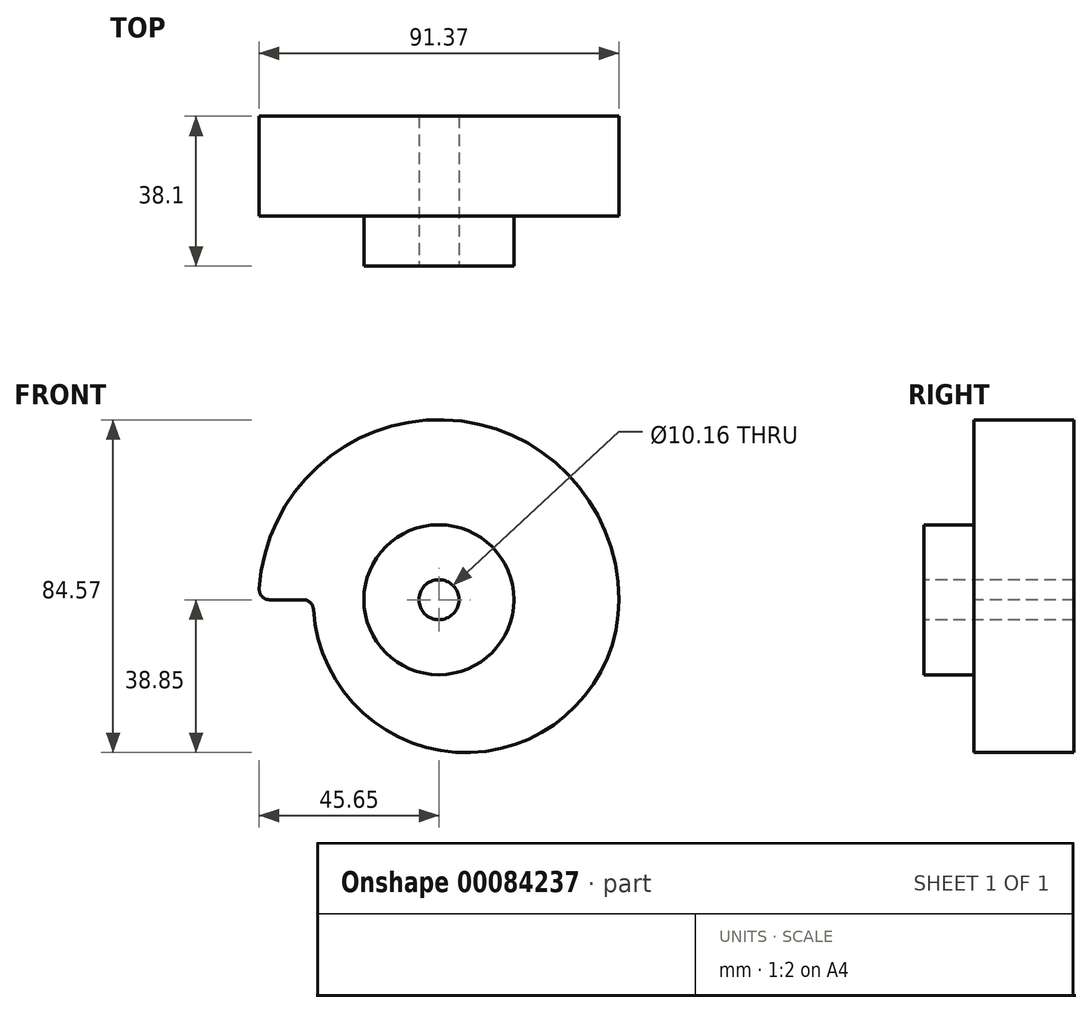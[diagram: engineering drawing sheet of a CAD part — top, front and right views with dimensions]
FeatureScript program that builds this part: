
annotation { "Feature Type Name" : "Feature", "Feature Type Description" : "" }
export const myFeature = defineFeature(function(context is Context, id is Id, definition is map)
    precondition{}
    {
        {
            var Q0;
            Q0=qCreatedBy(makeId("Front.planeOp"),FACE);
            var sketch = newSketch(context, id + "F0", { "sketchPlane" : qUnion([Q0])});
            skLineSegment(sketch, "E0", {"start": v(0, 0) * mm, "end": v(45.72, 0) * mm, "construction": true});
            skArc(sketch, "E1", {"start": v(45.72, 0) * mm, "mid": v(0, 45.72) * mm, "end": v(-45.72, 0) * mm});
            skArc(sketch, "E2", {"start": v(45.72, 0) * mm, "mid": v(6.87, -38.85) * mm, "end": v(-31.98, 0) * mm});
            skLineSegment(sketch, "E3", {"start": v(-31.98, 0) * mm, "end": v(0, 0) * mm, "construction": true});
            skLineSegment(sketch, "E4", {"start": v(-45.72, 0) * mm, "end": v(-31.98, 0) * mm});
            skSolve(sketch);
        }
        {
            var Q0;
            Q0=makeQuery(id+"F0.imprint","IMPRINT",FACE,{"disambiguationData":[TD([[makeQuery(id+"F0.imprint","IMPRINT",EDGE,{"derivedFrom":sQuery(id+"F0.wireOp",EDGE,"E1")}),1.0]])]});
            extrude(context, id + "F1", {"entities" : qUnion([Q0]), "depth" : 25.4 * mm});
        }
        {
            var Q0;
            Q0=makeQuery(id+"F1.opExtrude","CAP_FACE",FACE,{"disambiguationData":[OSD([sQuery(id+"F0.wireOp",EDGE,"E1"),sQuery(id+"F0.wireOp",EDGE,"E2"),sQuery(id+"F0.wireOp",EDGE,"E4")])],"isStart":false});
            var sketch = newSketch(context, id + "F2", { "sketchPlane" : qUnion([Q0])});
            skCircle(sketch, "E5.0", {"center": v(0, 0) * mm, "radius": 5.08 * mm});
            skSolve(sketch);
        }
        {
            var Q0;
            Q0 = qSketchRegion(id + "F2", true);
            extrude(context, id + "F3", {"entities" : qUnion([Q0]), "operationType" : NewBodyOperationType.REMOVE, "endBound" : BoundingType.SYMMETRIC, "oppositeDirection" : true, "depth" : 254 * mm});
        }
        {
            var Q0;
            Q0=makeQuery(id+"F1.opExtrude","SWEPT_EDGE",EDGE,{"disambiguationData":[OSD([sQuery(id+"F0.wireOp",EDGE,"E1"),sQuery(id+"F0.wireOp",EDGE,"E4")])]});
            fillet(context, id + "F4", {"entities" : qUnion([Q0]), "radius" : 2.54 * mm, "tangentPropagation" : true, "allowEdgeOverflow" : false});
        }
        {
            var Q0;
            Q0=makeQuery(id+"F1.opExtrude","SWEPT_EDGE",EDGE,{"disambiguationData":[OSD([sQuery(id+"F0.wireOp",EDGE,"E2"),sQuery(id+"F0.wireOp",EDGE,"E4")])]});
            fillet(context, id + "F5", {"entities" : qUnion([Q0]), "radius" : 2.54 * mm, "tangentPropagation" : true, "allowEdgeOverflow" : false});
        }
        {
            var Q0;
            Q0=makeQuery(id+"F1.opExtrude","CAP_FACE",FACE,{"disambiguationData":[OSD([sQuery(id+"F0.wireOp",EDGE,"E1"),sQuery(id+"F0.wireOp",EDGE,"E2"),sQuery(id+"F0.wireOp",EDGE,"E4")])],"isStart":false});
            var sketch = newSketch(context, id + "F6", { "sketchPlane" : qUnion([Q0])});
            skCircle(sketch, "E6", {"center": v(0, 0) * mm, "radius": 19.05 * mm});
            skSolve(sketch);
        }
        {
            var Q0;
            Q0=makeQuery(id+"F6.imprint","IMPRINT",FACE,{"disambiguationData":[TD([[makeQuery(id+"F6.imprint","IMPRINT",EDGE,{"derivedFrom":sQuery(id+"F6.wireOp",EDGE,"E6")}),1.0]])]});
            extrude(context, id + "F7", {"entities" : qUnion([Q0]), "operationType" : NewBodyOperationType.ADD, "depth" : 12.7 * mm});
        }
    });
